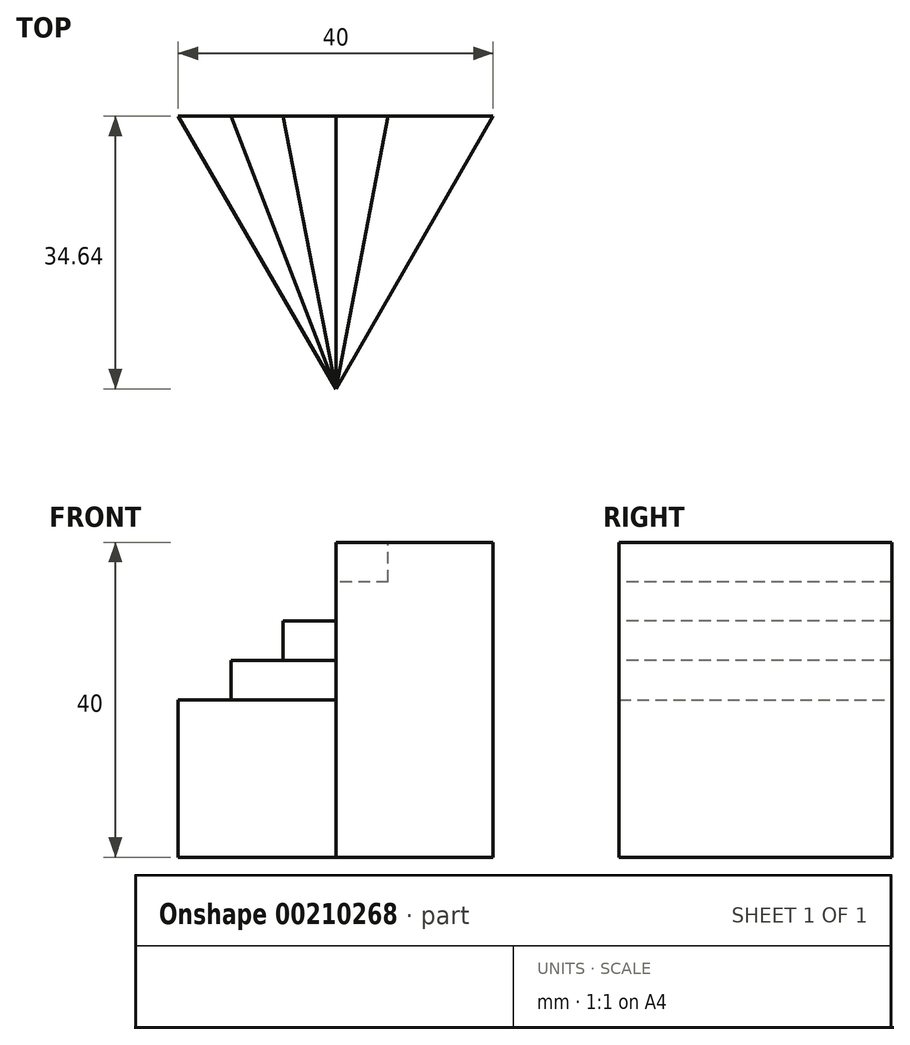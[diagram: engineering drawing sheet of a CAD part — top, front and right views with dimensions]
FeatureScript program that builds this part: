
annotation { "Feature Type Name" : "Feature", "Feature Type Description" : "" }
export const myFeature = defineFeature(function(context is Context, id is Id, definition is map)
    precondition{}
    {
        {
            var Q0;
            Q0=qCreatedBy(makeId("Top.planeOp"),FACE);
            var sketch = newSketch(context, id + "F0", { "sketchPlane" : qUnion([Q0])});
            skCircle(sketch, "E0.cCircle", {"center": v(0, 0) * mm, "radius": 11.55 * mm, "construction": true});
            skLineSegment(sketch, "E0.0", {"start": v(-20, 11.55) * mm, "end": v(20, 11.55) * mm});
            skLineSegment(sketch, "E0.1", {"start": v(20, 11.55) * mm, "end": v(0, -23.1) * mm});
            skLineSegment(sketch, "E0.2", {"start": v(0, -23.1) * mm, "end": v(-20, 11.55) * mm});
            skPoint(sketch, "E0.0.midPoint", {"position": v(0, 11.55) * mm});
            skSolve(sketch);
        }
        {
            var Q0;
            Q0=makeQuery(id+"F0.imprint","IMPRINT",FACE,{"disambiguationData":[TD([[makeQuery(id+"F0.imprint","IMPRINT",EDGE,{"derivedFrom":sQuery(id+"F0.wireOp",EDGE,"E0.0")}),-1.0]])]});
            extrude(context, id + "F1", {"entities" : qUnion([Q0]), "depth" : 40 * mm});
        }
        {
            var Q0;
            Q0=makeQuery(id+"F1.opExtrude","CAP_FACE",FACE,{"disambiguationData":[OSD([sQuery(id+"F0.wireOp",EDGE,"E0.0"),sQuery(id+"F0.wireOp",EDGE,"E0.1"),sQuery(id+"F0.wireOp",EDGE,"E0.2")])],"isStart":false});
            var sketch = newSketch(context, id + "F2", { "sketchPlane" : qUnion([Q0])});
            skLineSegment(sketch, "E1", {"start": v(-6.67, 11.55) * mm, "end": v(0, -23.1) * mm, "construction": true});
            skLineSegment(sketch, "E2", {"start": v(0, -23.1) * mm, "end": v(6.67, 11.55) * mm, "construction": true});
            skLineSegment(sketch, "E3", {"start": v(20, 11.55) * mm, "end": v(6.67, 11.55) * mm, "construction": true});
            skLineSegment(sketch, "E4", {"start": v(-6.67, 11.55) * mm, "end": v(-20, 11.55) * mm, "construction": true});
            skLineSegment(sketch, "E5", {"start": v(6.67, 11.55) * mm, "end": v(-6.67, 11.55) * mm, "construction": true});
            skSolve(sketch);
        }
        {
            var Q0;
            Q0=makeQuery(id+"F2.imprint","IMPRINT",FACE,{"disambiguationData":[TD([[makeQuery(id+"F2.imprint","IMPRINT",EDGE,{"derivedFrom":makeQuery(id+"F1.opExtrude","CAP_EDGE",EDGE,{"disambiguationData":[OSD([sQuery(id+"F0.wireOp",EDGE,"E0.0")])],"isStart":false})}),-1.0]])]});
            var sketch = newSketch(context, id + "F3", { "sketchPlane" : qUnion([Q0])});
            skLineSegment(sketch, "E6", {"start": v(6.67, 11.55) * mm, "end": v(0, -23.1) * mm});
            skLineSegment(sketch, "E7", {"start": v(0, -23.1) * mm, "end": v(-20, 11.55) * mm});
            skLineSegment(sketch, "E8", {"start": v(-20, 11.55) * mm, "end": v(6.67, 11.55) * mm});
            skSolve(sketch);
        }
        {
            var Q0;
            Q0 = qSketchRegion(id + "F3", true);
            extrude(context, id + "F4", {"entities" : qUnion([Q0]), "operationType" : NewBodyOperationType.REMOVE, "oppositeDirection" : true, "depth" : 10 * mm});
        }
        {
            var Q0;
            Q0=makeQuery(id+"F2.imprint","IMPRINT",FACE,{"disambiguationData":[TD([[makeQuery(id+"F2.imprint","IMPRINT",EDGE,{"derivedFrom":makeQuery(id+"F1.opExtrude","CAP_EDGE",EDGE,{"disambiguationData":[OSD([sQuery(id+"F0.wireOp",EDGE,"E0.0")])],"isStart":false})}),-1.0]])]});
            var sketch = newSketch(context, id + "F5", { "sketchPlane" : qUnion([Q0])});
            skLineSegment(sketch, "E9", {"start": v(-6.67, 11.55) * mm, "end": v(0, -23.1) * mm});
            skLineSegment(sketch, "E10", {"start": v(0, -23.1) * mm, "end": v(-20, 11.55) * mm});
            skLineSegment(sketch, "E11", {"start": v(-20, 11.55) * mm, "end": v(-6.67, 11.55) * mm});
            skSolve(sketch);
        }
        {
            var Q0;
            Q0 = qSketchRegion(id + "F5", true);
            extrude(context, id + "F6", {"entities" : qUnion([Q0]), "operationType" : NewBodyOperationType.REMOVE, "oppositeDirection" : true, "depth" : 20 * mm});
        }
        {
            var Q0;
            Q0=makeQuery(id+"F4.boolean.opBoolean","COPY",FACE,{"derivedFrom":makeQuery(id+"F4.opExtrude","CAP_FACE",FACE,{"disambiguationData":[OSD([sQuery(id+"F3.wireOp",EDGE,"E6"),sQuery(id+"F3.wireOp",EDGE,"E7"),sQuery(id+"F3.wireOp",EDGE,"E8")])],"isStart":false})});
            var sketch = newSketch(context, id + "F7", { "sketchPlane" : qUnion([Q0])});
            skLineSegment(sketch, "E12", {"start": v(0, -23.1) * mm, "end": v(0, 11.55) * mm});
            skLineSegment(sketch, "E13", {"start": v(0, 11.55) * mm, "end": v(6.67, 11.55) * mm});
            skLineSegment(sketch, "E14", {"start": v(6.67, 11.55) * mm, "end": v(0, -23.1) * mm});
            skSolve(sketch);
        }
        {
            var Q0;
            Q0 = qSketchRegion(id + "F7", true);
            extrude(context, id + "F8", {"entities" : qUnion([Q0]), "operationType" : NewBodyOperationType.ADD, "depth" : 5 * mm});
        }
        {
            var Q0;
            Q0=makeQuery(id+"F6.boolean.opBoolean","COPY",FACE,{"derivedFrom":makeQuery(id+"F6.opExtrude","CAP_FACE",FACE,{"disambiguationData":[OSD([sQuery(id+"F5.wireOp",EDGE,"E9"),sQuery(id+"F5.wireOp",EDGE,"E10"),sQuery(id+"F5.wireOp",EDGE,"E11")])],"isStart":false})});
            var sketch = newSketch(context, id + "F9", { "sketchPlane" : qUnion([Q0])});
            skLineSegment(sketch, "E15", {"start": v(-13.33, 11.55) * mm, "end": v(0, -23.1) * mm});
            skLineSegment(sketch, "E16", {"start": v(0, -23.1) * mm, "end": v(-6.67, 11.55) * mm});
            skLineSegment(sketch, "E17", {"start": v(-6.67, 11.55) * mm, "end": v(-13.33, 11.55) * mm});
            skSolve(sketch);
        }
        {
            var Q0;
            Q0 = qSketchRegion(id + "F9", true);
            extrude(context, id + "F10", {"entities" : qUnion([Q0]), "operationType" : NewBodyOperationType.ADD, "depth" : 5 * mm});
        }
    });
